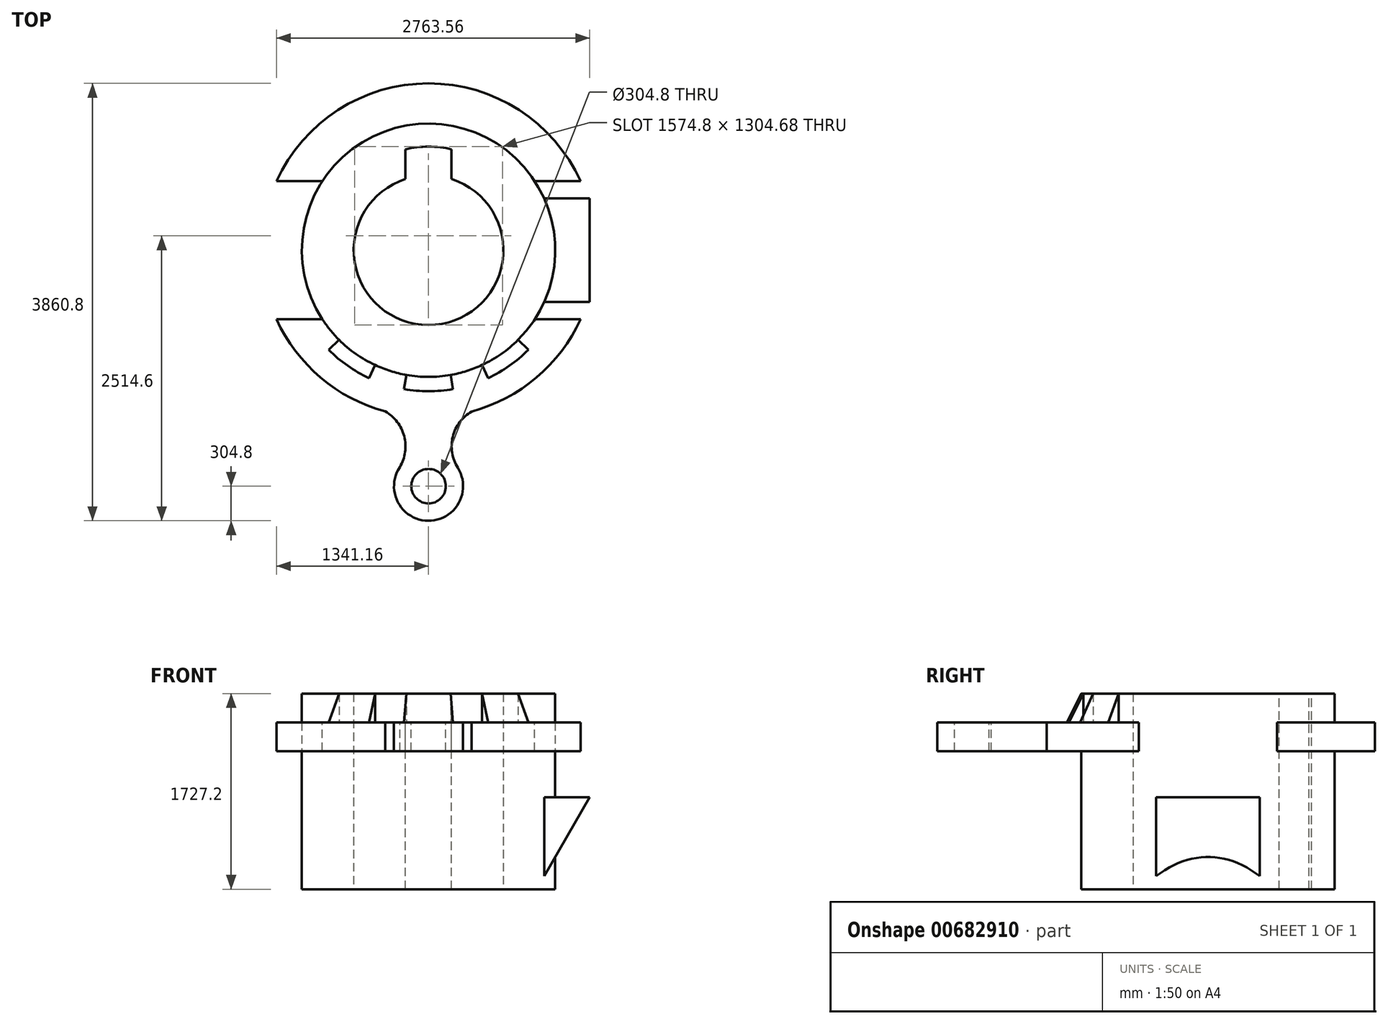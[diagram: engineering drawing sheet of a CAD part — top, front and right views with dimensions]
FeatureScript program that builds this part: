
annotation { "Feature Type Name" : "Feature", "Feature Type Description" : "" }
export const myFeature = defineFeature(function(context is Context, id is Id, definition is map)
    precondition{}
    {
        {
            var Q0;
            Q0=qCreatedBy(makeId("Top.planeOp"),FACE);
            var sketch = newSketch(context, id + "F0", { "sketchPlane" : qUnion([Q0])});
            skCircle(sketch, "E0", {"center": v(0, 0) * mm, "radius": 1117.6 * mm});
            skSolve(sketch);
        }
        {
            var Q0;
            Q0=makeQuery(id+"F0.imprint","IMPRINT",FACE,{"disambiguationData":[TD([[makeQuery(id+"F0.imprint","IMPRINT",EDGE,{"derivedFrom":sQuery(id+"F0.wireOp",EDGE,"E0")}),1.0]])]});
            extrude(context, id + "F1", {"entities" : qUnion([Q0]), "depth" : 1473.2 * mm, "offsetDistance" : 25.4 * mm});
        }
        {
            var Q0;
            Q0=makeQuery(id+"F1.opExtrude","CAP_FACE",FACE,{"disambiguationData":[OSD([sQuery(id+"F0.wireOp",EDGE,"E0")])],"isStart":false});
            var sketch = newSketch(context, id + "F2", { "sketchPlane" : qUnion([Q0])});
            skCircle(sketch, "E1", {"center": v(0, 0) * mm, "radius": 1473.2 * mm});
            skSolve(sketch);
        }
        {
            var Q0;
            {var subQ0=sQuery(id+"F0.wireOp",EDGE,"E0");Q0=makeQuery(id+"F4.boolean.opBoolean","MERGE",FACE,{"derivedFrom":[makeQuery(id+"F1.opExtrude","CAP_FACE",FACE,{"disambiguationData":[OSD([subQ0])],"isStart":false}),makeQuery(id+"F4.opExtrude","CAP_FACE",FACE,{"disambiguationData":[OSD([subQ0,sQuery(id+"F2.wireOp",EDGE,"E1")])],"isStart":true})]});}
            var sketch = newSketch(context, id + "F3", { "sketchPlane" : qUnion([Q0])});
            skCircle(sketch, "E2", {"center": v(0, 0) * mm, "radius": 1117.6 * mm});
            skLineSegment(sketch, "E3", {"start": v(936.7, 609.6) * mm, "end": v(1341.16, 609.6) * mm});
            skLineSegment(sketch, "E4", {"start": v(936.7, -609.6) * mm, "end": v(1341.16, -609.6) * mm});
            skLineSegment(sketch, "E5", {"start": v(-936.7, 609.6) * mm, "end": v(-1341.16, 609.6) * mm});
            skLineSegment(sketch, "E6", {"start": v(-936.7, -609.6) * mm, "end": v(-1341.16, -609.6) * mm});
            skLineSegment(sketch, "E7", {"start": v(0, 0) * mm, "end": v(0, -2082.8) * mm});
            skCircle(sketch, "E8", {"center": v(0, -2082.8) * mm, "radius": 152.4 * mm});
            skCircle(sketch, "E9", {"center": v(0, -2082.8) * mm, "radius": 304.8 * mm});
            skArc(sketch, "E10", {"start": v(380.38, -1423.24) * mm, "mid": v(213.52, -1645.78) * mm, "end": v(257.9, -1920.36) * mm});
            skCircle(sketch, "E11", {"center": v(0, 0) * mm, "radius": 660.4 * mm});
            skCircle(sketch, "E12.0.0", {"center": v(0, 0) * mm, "radius": 1473.2 * mm});
            skArc(sketch, "E13", {"start": v(-253.55, -1913.63) * mm, "mid": v(-214.72, -1641.43) * mm, "end": v(-381.62, -1422.92) * mm});
            skSolve(sketch);
        }
        {
            var Q0;
            Q0=makeQuery(id+"F2.imprint","IMPRINT",FACE,{"disambiguationData":[TD([[makeQuery(id+"F2.imprint","IMPRINT",EDGE,{"derivedFrom":sQuery(id+"F2.wireOp",EDGE,"E1")}),1.0]])]});
            var Q1;
            {var subQ5=sQuery(id+"F3.wireOp",EDGE,"E10");Q1=makeQuery(id+"F3.imprint","IMPRINT",FACE,{"disambiguationData":[TD([[makeQuery(id+"F3.imprint","IMPRINT",EDGE,{"derivedFrom":subQ5}),-1.0]])]});}
            var Q2;
            {var subQ5=sQuery(id+"F3.wireOp",EDGE,"E13");Q2=makeQuery(id+"F3.imprint","IMPRINT",FACE,{"disambiguationData":[TD([[makeQuery(id+"F3.imprint","IMPRINT",EDGE,{"derivedFrom":subQ5}),-1.0]])]});}
            var Q3;
            Q3=makeQuery(id+"F3.imprint","IMPRINT",FACE,{"disambiguationData":[TD([[makeQuery(id+"F3.imprint","IMPRINT",EDGE,{"derivedFrom":sQuery(id+"F3.wireOp",EDGE,"E8")}),-1.0]])]});
            extrude(context, id + "F4", {"entities" : qUnion([Q0, Q1, Q2, Q3]), "operationType" : NewBodyOperationType.ADD, "oppositeDirection" : true, "depth" : 254 * mm, "offsetDistance" : 25.4 * mm});
        }
        {
            var Q0;
            {var subQ0=sQuery(id+"F3.wireOp",EDGE,"E5");Q0=makeQuery(id+"F3.imprint","IMPRINT",FACE,{"disambiguationData":[TD([[makeQuery(id+"F3.imprint","IMPRINT",EDGE,{"derivedFrom":subQ0}),1.0]])]});}
            var Q1;
            {var subQ0=sQuery(id+"F3.wireOp",EDGE,"E3");Q1=makeQuery(id+"F3.imprint","IMPRINT",FACE,{"disambiguationData":[TD([[makeQuery(id+"F3.imprint","IMPRINT",EDGE,{"derivedFrom":subQ0}),-1.0]])]});}
            extrude(context, id + "F5", {"entities" : qUnion([Q0, Q1]), "operationType" : NewBodyOperationType.REMOVE, "oppositeDirection" : true, "depth" : 254 * mm, "offsetDistance" : 25.4 * mm});
        }
        {
            var Q0;
            {var subQ0=sQuery(id+"F3.wireOp",EDGE,"E2");var subQ11=makeQuery(id+"F3.imprint","INTERSECT",VERTEX,{"derivedFrom":[subQ0,sQuery(id+"F3.wireOp",EDGE,"E3")]});Q0=makeQuery(id+"F3.imprint","IMPRINT",FACE,{"disambiguationData":[TD([[makeQuery(id+"F3.imprint","IMPRINT",EDGE,{"disambiguationData":[TD([[subQ11,-1.0]])],"derivedFrom":subQ0}),1.0]])]});}
            var Q1;
            {var subQ0=sQuery(id+"F3.wireOp",EDGE,"pez8YJvT-IcjL-SYWB-lp8Q-WMLA7dvs1uYD");Q1=makeQuery(id+"F3.imprint","IMPRINT",FACE,{"disambiguationData":[TD([[makeQuery(id+"F3.imprint","IMPRINT",EDGE,{"derivedFrom":subQ0}),1.0]])]});}
            var Q2;
            {var subQ0=sQuery(id+"F3.wireOp",EDGE,"pez8YJvT-IcjL-SYWB-lp8Q-WMLA7dvs1uYD");Q2=makeQuery(id+"F3.imprint","IMPRINT",FACE,{"disambiguationData":[TD([[makeQuery(id+"F3.imprint","IMPRINT",EDGE,{"derivedFrom":subQ0}),-1.0]])]});}
            var Q3;
            {var subQ0=sQuery(id+"F3.wireOp",EDGE,"E7");var subQ1=sQuery(id+"F3.wireOp",EDGE,"E2");var subQ2=makeQuery(id+"F3.imprint","INTERSECT",VERTEX,{"derivedFrom":[subQ1,subQ0]});Q3=makeQuery(id+"F3.imprint","IMPRINT",FACE,{"disambiguationData":[TD([[makeQuery(id+"F3.imprint","IMPRINT",EDGE,{"disambiguationData":[TD([[subQ2,-1.0]])],"derivedFrom":subQ1}),1.0]])]});}
            extrude(context, id + "F6", {"entities" : qUnion([Q0, Q1, Q2, Q3]), "operationType" : NewBodyOperationType.ADD, "depth" : 254 * mm, "offsetDistance" : 25.4 * mm});
        }
        {
            var Q0;
            Q0=makeQuery(id+"F6.opExtrude","CAP_FACE",FACE,{"disambiguationData":[OSD([sQuery(id+"F3.wireOp",EDGE,"E2")])],"isStart":false});
            var sketch = newSketch(context, id + "F7", { "sketchPlane" : qUnion([Q0])});
            skCircle(sketch, "E14", {"center": v(0, 0) * mm, "radius": 660.4 * mm});
            skLineSegment(sketch, "E15", {"start": v(0, 0) * mm, "end": v(0, 660.4) * mm});
            skCircle(sketch, "E16", {"center": v(0, 0) * mm, "radius": 914.4 * mm});
            skLineSegment(sketch, "E17", {"start": v(203.2, 891.54) * mm, "end": v(203.2, 628.36) * mm});
            skLineSegment(sketch, "E18", {"start": v(-203.2, 891.54) * mm, "end": v(-203.2, 628.36) * mm});
            skLineSegment(sketch, "E19", {"start": v(0, 0) * mm, "end": v(0, -914.4) * mm});
            skCircle(sketch, "E20.0", {"center": v(0, 0) * mm, "radius": 1117.6 * mm});
            skLineSegment(sketch, "E21", {"start": v(0, 0) * mm, "end": v(-472.32, -1012.89) * mm});
            skLineSegment(sketch, "E22", {"start": v(0, 0) * mm, "end": v(-790.26, -790.26) * mm});
            skLineSegment(sketch, "E23", {"start": v(0, 0) * mm, "end": v(-194.07, -1100.62) * mm});
            skLineSegment(sketch, "E24", {"start": v(0, 0) * mm, "end": v(194.07, -1100.62) * mm});
            skLineSegment(sketch, "E25", {"start": v(0, 0) * mm, "end": v(472.32, -1012.89) * mm});
            skLineSegment(sketch, "E26", {"start": v(0, 0) * mm, "end": v(790.26, -790.26) * mm});
            skLineSegment(sketch, "E27", {"start": v(957.71, 576.03) * mm, "end": v(939.38, -605.47) * mm});
            skLineSegment(sketch, "E28", {"start": v(0, 0) * mm, "end": v(1016, 0) * mm});
            skSolve(sketch);
        }
        {
            var Q0;
            {var subQ0=sQuery(id+"F7.wireOp",EDGE,"E17");Q0=makeQuery(id+"F7.imprint","IMPRINT",FACE,{"disambiguationData":[TD([[makeQuery(id+"F7.imprint","IMPRINT",EDGE,{"derivedFrom":subQ0}),-1.0]])]});}
            var Q1;
            {var subQ0=sQuery(id+"F7.wireOp",EDGE,"E15");Q1=makeQuery(id+"F7.imprint","IMPRINT",FACE,{"disambiguationData":[TD([[makeQuery(id+"F7.imprint","IMPRINT",EDGE,{"derivedFrom":subQ0}),1.0]])]});}
            var Q2;
            {var subQ4=sQuery(id+"F7.wireOp",EDGE,"E15");Q2=makeQuery(id+"F7.imprint","IMPRINT",FACE,{"disambiguationData":[TD([[makeQuery(id+"F7.imprint","IMPRINT",EDGE,{"derivedFrom":subQ4}),-1.0]])]});}
            var Q3;
            {var subQ0=sQuery(id+"F7.wireOp",EDGE,"Rn6lizgL-IEuc-7Tkr-UscK-9PhkPfJaQyf1");var subQ1=sQuery(id+"F7.wireOp",EDGE,"E14");var subQ2=makeQuery(id+"F7.imprint","INTERSECT",VERTEX,{"derivedFrom":[subQ1,subQ0]});Q3=makeQuery(id+"F7.imprint","IMPRINT",FACE,{"disambiguationData":[TD([[makeQuery(id+"F7.imprint","IMPRINT",EDGE,{"disambiguationData":[TD([[subQ2,1.0]])],"derivedFrom":subQ1}),1.0]])]});}
            var Q4;
            {var subQ0=sQuery(id+"F7.wireOp",EDGE,"TZzxt7bj-SH1H-Iq0q-f9En-1LoxKDuLfApB");Q4=makeQuery(id+"F7.imprint","IMPRINT",FACE,{"disambiguationData":[TD([[makeQuery(id+"F7.imprint","IMPRINT",EDGE,{"derivedFrom":subQ0}),1.0]])]});}
            var Q5;
            {var subQ0=sQuery(id+"F7.wireOp",EDGE,"E28");var subQ1=sQuery(id+"F7.wireOp",EDGE,"E14");var subQ2=makeQuery(id+"F7.imprint","INTERSECT",VERTEX,{"derivedFrom":[subQ1,subQ0]});Q5=makeQuery(id+"F7.imprint","IMPRINT",FACE,{"disambiguationData":[TD([[makeQuery(id+"F7.imprint","IMPRINT",EDGE,{"disambiguationData":[TD([[subQ2,1.0]])],"derivedFrom":subQ1}),1.0]])]});}
            var Q6;
            {var subQ0=sQuery(id+"F7.wireOp",EDGE,"E25");var subQ1=sQuery(id+"F7.wireOp",EDGE,"E14");var subQ2=makeQuery(id+"F7.imprint","INTERSECT",VERTEX,{"derivedFrom":[subQ1,subQ0]});Q6=makeQuery(id+"F7.imprint","IMPRINT",FACE,{"disambiguationData":[TD([[makeQuery(id+"F7.imprint","IMPRINT",EDGE,{"disambiguationData":[TD([[subQ2,-1.0]])],"derivedFrom":subQ1}),1.0]])]});}
            var Q7;
            {var subQ0=sQuery(id+"F7.wireOp",EDGE,"E24");var subQ1=sQuery(id+"F7.wireOp",EDGE,"E14");var subQ2=makeQuery(id+"F7.imprint","INTERSECT",VERTEX,{"derivedFrom":[subQ1,subQ0]});Q7=makeQuery(id+"F7.imprint","IMPRINT",FACE,{"disambiguationData":[TD([[makeQuery(id+"F7.imprint","IMPRINT",EDGE,{"disambiguationData":[TD([[subQ2,-1.0]])],"derivedFrom":subQ1}),1.0]])]});}
            var Q8;
            {var subQ0=sQuery(id+"F7.wireOp",EDGE,"E19");var subQ1=sQuery(id+"F7.wireOp",EDGE,"E14");var subQ2=makeQuery(id+"F7.imprint","INTERSECT",VERTEX,{"derivedFrom":[subQ1,subQ0]});Q8=makeQuery(id+"F7.imprint","IMPRINT",FACE,{"disambiguationData":[TD([[makeQuery(id+"F7.imprint","IMPRINT",EDGE,{"disambiguationData":[TD([[subQ2,-1.0]])],"derivedFrom":subQ1}),1.0]])]});}
            var Q9;
            {var subQ0=sQuery(id+"F7.wireOp",EDGE,"E21");var subQ1=sQuery(id+"F7.wireOp",EDGE,"E14");var subQ2=makeQuery(id+"F7.imprint","INTERSECT",VERTEX,{"derivedFrom":[subQ1,subQ0]});Q9=makeQuery(id+"F7.imprint","IMPRINT",FACE,{"disambiguationData":[TD([[makeQuery(id+"F7.imprint","IMPRINT",EDGE,{"disambiguationData":[TD([[subQ2,-1.0]])],"derivedFrom":subQ1}),1.0]])]});}
            var Q10;
            {var subQ0=sQuery(id+"F7.wireOp",EDGE,"E22");var subQ1=sQuery(id+"F7.wireOp",EDGE,"E14");var subQ2=makeQuery(id+"F7.imprint","INTERSECT",VERTEX,{"derivedFrom":[subQ1,subQ0]});Q10=makeQuery(id+"F7.imprint","IMPRINT",FACE,{"disambiguationData":[TD([[makeQuery(id+"F7.imprint","IMPRINT",EDGE,{"disambiguationData":[TD([[subQ2,-1.0]])],"derivedFrom":subQ1}),1.0]])]});}
            var Q11;
            {var subQ0=sQuery(id+"F7.wireOp",EDGE,"E23");var subQ1=sQuery(id+"F7.wireOp",EDGE,"E14");var subQ2=makeQuery(id+"F7.imprint","INTERSECT",VERTEX,{"derivedFrom":[subQ1,subQ0]});Q11=makeQuery(id+"F7.imprint","IMPRINT",FACE,{"disambiguationData":[TD([[makeQuery(id+"F7.imprint","IMPRINT",EDGE,{"disambiguationData":[TD([[subQ2,-1.0]])],"derivedFrom":subQ1}),1.0]])]});}
            extrude(context, id + "F8", {"entities" : qUnion([Q0, Q1, Q2, Q3, Q4, Q5, Q6, Q7, Q8, Q9, Q10, Q11]), "operationType" : NewBodyOperationType.REMOVE, "oppositeDirection" : true, "depth" : 1727.2 * mm, "offsetDistance" : 25.4 * mm});
        }
        {
            var Q0;
            {var subQ2=sQuery(id+"F2.wireOp",EDGE,"E1");var subQ3=sQuery(id+"F3.wireOp",EDGE,"E4");var subQ4=sQuery(id+"F0.wireOp",EDGE,"E0");Q0=makeQuery(id+"F6.boolean.opBoolean","SPLIT",FACE,{"disambiguationData":[TD([makeQuery(id+"F5.boolean.opBoolean","COPY",FACE,{"derivedFrom":makeQuery(id+"F5.opExtrude","SWEPT_FACE",FACE,{"disambiguationData":[OSD([subQ3])]})})])],"derivedFrom":makeQuery(id+"F4.boolean.opBoolean","MERGE",FACE,{"derivedFrom":[makeQuery(id+"F1.opExtrude","CAP_FACE",FACE,{"disambiguationData":[OSD([subQ4])],"isStart":false}),makeQuery(id+"F4.opExtrude","CAP_FACE",FACE,{"disambiguationData":[OSD([subQ4,subQ2])],"isStart":true})]})});}
            var sketch = newSketch(context, id + "F9", { "sketchPlane" : qUnion([Q0])});
            skCircle(sketch, "E29", {"center": v(0, 0) * mm, "radius": 1244.6 * mm});
            skLineSegment(sketch, "E30", {"start": v(-472.32, -1012.89) * mm, "end": v(-526, -1128) * mm});
            skLineSegment(sketch, "E31", {"start": v(-790.26, -790.26) * mm, "end": v(-880.07, -880.07) * mm});
            skPoint(sketch, "E32.0.end.orphan", {"position": v(-790.26, -790.26) * mm});
            skPoint(sketch, "E33.0.end.orphan", {"position": v(-472.32, -1012.89) * mm});
            skArc(sketch, "E34.0", {"start": v(-790.26, -790.26) * mm, "mid": v(116.28, -1111.53) * mm, "end": v(936.7, -609.6) * mm});
            skPoint(sketch, "E35.orphan", {"position": v(-936.7, -609.6) * mm});
            skLineSegment(sketch, "E36", {"start": v(-194.07, -1100.62) * mm, "end": v(-216.12, -1225.7) * mm});
            skLineSegment(sketch, "E37", {"start": v(194.07, -1100.62) * mm, "end": v(216.12, -1225.7) * mm});
            skLineSegment(sketch, "E38", {"start": v(472.32, -1012.89) * mm, "end": v(526, -1128) * mm});
            skLineSegment(sketch, "E39", {"start": v(790.26, -790.26) * mm, "end": v(880.07, -880.07) * mm});
            skPoint(sketch, "E40.0.end.orphan", {"position": v(-194.07, -1100.62) * mm});
            skPoint(sketch, "E41.0.end.orphan", {"position": v(194.07, -1100.62) * mm});
            skPoint(sketch, "E42.0.end.orphan", {"position": v(472.32, -1012.89) * mm});
            skPoint(sketch, "E43.0.end.orphan", {"position": v(790.26, -790.26) * mm});
            skSolve(sketch);
        }
        {
            var Q0;
            {var subQ0=sQuery(id+"F9.wireOp",EDGE,"E30");Q0=makeQuery(id+"F9.imprint","IMPRINT",FACE,{"disambiguationData":[TD([[makeQuery(id+"F9.imprint","IMPRINT",EDGE,{"derivedFrom":subQ0}),-1.0]])]});}
            var Q1;
            {var subQ0=sQuery(id+"F9.wireOp",EDGE,"E36");Q1=makeQuery(id+"F9.imprint","IMPRINT",FACE,{"disambiguationData":[TD([[makeQuery(id+"F9.imprint","IMPRINT",EDGE,{"derivedFrom":subQ0}),1.0]])]});}
            var Q2;
            {var subQ0=sQuery(id+"F9.wireOp",EDGE,"E38");Q2=makeQuery(id+"F9.imprint","IMPRINT",FACE,{"disambiguationData":[TD([[makeQuery(id+"F9.imprint","IMPRINT",EDGE,{"derivedFrom":subQ0}),1.0]])]});}
            extrude(context, id + "F10", {"entities" : qUnion([Q0, Q1, Q2]), "operationType" : NewBodyOperationType.ADD, "depth" : 254 * mm, "offsetDistance" : 25.4 * mm});
        }
        {
            var Q0;
            Q0=makeQuery(id+"F10.opExtrude","SWEPT_FACE",FACE,{"disambiguationData":[OSD([sQuery(id+"F9.wireOp",EDGE,"E30")])]});
            var sketch = newSketch(context, id + "F11", { "sketchPlane" : qUnion([Q0])});
            skLineSegment(sketch, "E44", {"start": v(-1117.6, 1727.2) * mm, "end": v(-1244.6, 1473.2) * mm});
            skPoint(sketch, "E45.0.end.orphan", {"position": v(1117.6, 1727.2) * mm});
            skPoint(sketch, "E45.0.start.orphan", {"position": v(-1117.6, 1727.2) * mm});
            skSolve(sketch);
        }
        {
            var Q0;
            Q0=makeQuery(id+"F11.imprint","IMPRINT",FACE,{"disambiguationData":[TD([[makeQuery(id+"F11.imprint","IMPRINT",EDGE,{"derivedFrom":sQuery(id+"F11.wireOp",EDGE,"E44")}),-1.0]])]});
            var Q1;
            Q1=sQuery(id+"F7.wireOp",EDGE,"E20.0");
            sweep(context, id + "F12", {"operationType" : NewBodyOperationType.REMOVE, "profiles" : qUnion([Q0]), "path" : qUnion([Q1])});
        }
        {
            var Q0;
            Q0=sQuery(id+"F7.wireOp",VERTEX,"E28.end");
            var Q1;
            Q1=sQuery(id+"F7.wireOp",EDGE,"E28");
            cPlane(context, id + "F13", {"entities" : qUnion([Q0, Q1]), "cplaneType" : CPlaneType.LINE_POINT, "offset" : 25.4 * mm, "width" : 152.4 * mm, "height" : 152.4 * mm});
        }
        {
            var Q0;
            Q0=qCreatedBy(id+"F13.planeOp",FACE);
            var sketch = newSketch(context, id + "F14", { "sketchPlane" : qUnion([Q0])});
            skPoint(sketch, "E46.0", {"position": v(0, 1727.2) * mm});
            skLineSegment(sketch, "E47", {"start": v(-457.2, 812.8) * mm, "end": v(457.2, 812.8) * mm});
            skLineSegment(sketch, "E48", {"start": v(-457.2, 812.8) * mm, "end": v(-457.2, 115.48) * mm});
            skLineSegment(sketch, "E49", {"start": v(-457.2, 115.48) * mm, "end": v(457.2, 115.48) * mm});
            skLineSegment(sketch, "E50", {"start": v(457.2, 812.8) * mm, "end": v(457.2, 115.48) * mm});
            skPoint(sketch, "E51.orphan", {"position": v(479.32, 115.48) * mm});
            skSolve(sketch);
        }
        {
            var Q0;
            Q0 = qSketchRegion(id + "F14", true);
            extrude(context, id + "F15", {"entities" : qUnion([Q0]), "operationType" : NewBodyOperationType.ADD, "depth" : 406.4 * mm, "offsetDistance" : 25.4 * mm});
        }
        {
            var Q0;
            Q0=makeQuery(id+"F15.opExtrude","SWEPT_FACE",FACE,{"disambiguationData":[OSD([sQuery(id+"F14.wireOp",EDGE,"E50")])]});
            var sketch = newSketch(context, id + "F16", { "sketchPlane" : qUnion([Q0])});
            skLineSegment(sketch, "E52.0", {"start": v(-1019.8, 812.8) * mm, "end": v(-1422.4, 812.8) * mm});
            skLineSegment(sketch, "E53", {"start": v(-1422.4, 812.8) * mm, "end": v(-1422.4, 812.8) * mm});
            skLineSegment(sketch, "E54.0", {"start": v(-1019.8, 812.8) * mm, "end": v(-1019.8, 812.8) * mm});
            skLineSegment(sketch, "E55.0", {"start": v(-1422.4, 115.48) * mm, "end": v(-1019.8, 115.48) * mm});
            skLineSegment(sketch, "E56", {"start": v(-1019.8, 812.8) * mm, "end": v(-1019.8, 115.48) * mm});
            skLineSegment(sketch, "E57", {"start": v(-1422.4, 812.8) * mm, "end": v(-1019.8, 115.48) * mm});
            skSolve(sketch);
        }
        {
            var Q0;
            Q0=makeQuery(id+"F16.imprint","IMPRINT",FACE,{"disambiguationData":[TD([[makeQuery(id+"F16.imprint","IMPRINT",EDGE,{"derivedFrom":sQuery(id+"F16.wireOp",EDGE,"E55.0")}),1.0]])]});
            extrude(context, id + "F17", {"entities" : qUnion([Q0]), "operationType" : NewBodyOperationType.REMOVE, "endBound" : BoundingType.UP_TO_NEXT, "oppositeDirection" : true, "depth" : 914.4 * mm, "offsetDistance" : 25.4 * mm});
        }
        {
            var Q0;
            Q0=makeQuery(id+"F17.boolean.opBoolean","COPY",FACE,{"derivedFrom":makeQuery(id+"F17.opExtrude","SWEPT_FACE",FACE,{"disambiguationData":[OSD([sQuery(id+"F16.wireOp",EDGE,"E55.0")])]})});
            extrude(context, id + "F18", {"entities" : qUnion([Q0]), "operationType" : NewBodyOperationType.ADD, "depth" : 177.8 * mm, "offsetDistance" : 25.4 * mm});
        }
    });
